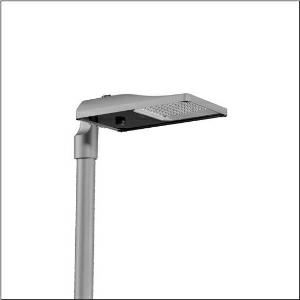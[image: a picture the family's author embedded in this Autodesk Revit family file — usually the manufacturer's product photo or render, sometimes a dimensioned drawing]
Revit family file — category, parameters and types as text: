
# Revit family: streetlight_sl_31_midi___st0_5a_5xh7b31t08na_48dc
name_source: partatom
category: Lighting Fixtures
units: mm (PartAtom-declared; Revit-internal decimal feet)

## family parameters
Cut with Voids When Loaded = No
Host = Face
Light Source = No
Part Type = Normal
Room Calculation Point = No
Round Connector Dimension = Use Diameter
Shared = No

## types (1)
- --- (1 x LED, 22750 lm, 149.5 W, 3000K)
    Apparent Load = 149 VA
    CIE Flux Codes = 43 76 97 100 100
    Color Rendering = 70
    Color Temperature = 3000K
    Default Elevation = 1800 mm
    Description = Streetlight SL 31 midi D4i, Desk-Remote mast luminaire for post-top, side-entry; light control with lens of PMMA; light distribution: ST0.5a, direct asymmetric distribution, for standard-compliant lighting for roads and squares; LED: luminous flux: 22.750lm, light colour: 730, colour temperature: 3000K; luminous efficacy: 152,2lm/W; control: pre-setting: logarithmic dimming characteristic, flexible luminous flux parameterisation, time-dependent luminous flux control, constant luminous flux control, power reduction, intelligent temperature release in ECG and LED module, overheat protection; luminaire housing, of diecast aluminium, Siteco® metallic grey (DB 702S), corrosivity category C5 high according to DIN EN ISO 12944; cover of toughened safety glass, transparent, opened without tools; mast flange of diecast aluminium, Siteco® metallic grey (DB 702S), spigot size: 76/60mm, mast flange included unmounted; with cable H07RN-F 2x 1.5mm², cable length: 12,5m, connection cable pre-assembled; mains connection: 220..240V, AC, 50/60Hz; power consumption (at start of service life): 149,5W / (at end of service life): 163,6W / (with reduced operation 50%): 66,6W; protection rating (complete): IP66; insulation class (complete): insulation class II (safety insulation); impact resistance: IK09; certification: CE, ENEC, ENEC+, VDE, UKCA, ZD4i; permissible operating ambient temperature for outdoor applications: -40..+50°C; packaging unit: 1 piece

Light Distribution: ST0.5a
    Height = 79 mm
    Lamp = 1 x LED
    Lamp Light Flux = 22750 lm
    Lamp Power = 149.5 W
    Lamp count = 1
    Length = 577 mm
    Luminous efficacy = 152 lm/W
    Manufacturer = Siteco
    ModVariant = No
    Model = 5XH7B31T08NA
    Number of Poles = 1
    OnlyDefault = Yes
    Power Factor = 1
    Product Name = Streetlight SL 31 midi | ST0.5a
    Product group = mast luminaire | pylon top
    ProductGroupID = 6100
    Protection Class = Protection class II
    Protection Degree = IP 66
    RLX_Detail_Level = 1
    RLX_Emergency_Light_Flux = 0 lm
    RLX_Emergency_Type = 0
    RLX_Emergency_Type_DB = No
    RlxData = <blob elided: 54129 chars, md5=377166ed>
    Socket = socket
    Standby Power = 0 W
    System Light Flux = 22749 lm
    System Power = 149 W
    Type Comments = factory setting: luminous flux: 100 % | dim-lin: 254 | 795 mA
    Type Image = l_1300321.jpg
    URL = http://relux.com
    VarID = @adj_054494
    Voltage = 0 V
    Weight = 0.00 kg
    Width = 362 mm

## geometry (parser evidence)
native form markers: Blend x4, Sweep x11
no freeform markers — native parametric forms only
